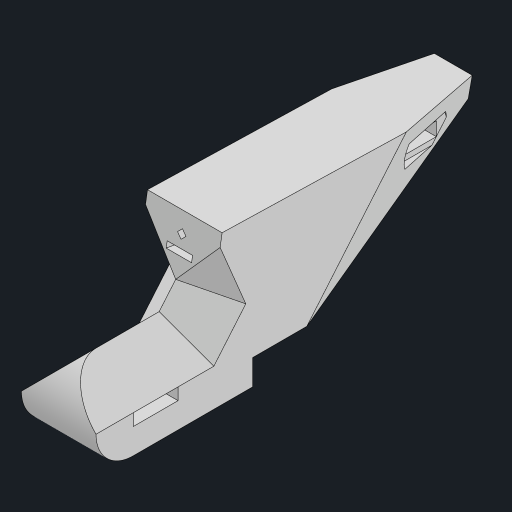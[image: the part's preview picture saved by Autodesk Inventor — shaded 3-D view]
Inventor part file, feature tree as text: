
AUTODESK INVENTOR PART (.ipt)
format: ipt  version: 2023 (Build 270158000, 158)  size: 356,352 bytes
history: native  units: mm
features: extrude x16, sketch x14, other x10, projected_geometry x4
ambient origin geometry x8: Origin, YZ Plane, XZ Plane, XY Plane, X Axis, Y Axis, Z Axis, Center Point
bodies: Body1 (feature_tree)
feature tree (44):
  other  "ソリッド1"
  extrude  "押し出し1"  Depth=0.261799mm
  other  "作業平面1"
  other  "作業平面3"
  extrude  "押し出し5"  Depth=37.0mm
  extrude  "押し出し6"  Depth=25.0mm
  other  "おでこ"
  other  "作業平面4"
  extrude  "押し出し7"  Depth=22.68928mm
  other  "作業平面5"
  extrude  "押し出し8"  Depth=1.658063mm
  extrude  "押し出し9"  Depth=60.0mm
  other  "作業平面9"
  extrude  "押し出し16"  Depth=3.0mm
  other  "作業平面11"
  extrude  "押し出し11"  Depth=80.0mm
  extrude  "押し出し12"  Depth=180.0mm
  extrude  "押し出し13"  Depth=25.0mm
  extrude  "押し出し15"  Depth=5.0mm
  extrude  "貫通"  Depth=180.0mm
  extrude  "25mm"  Depth=15.0mm
  other  "作業平面12"
  extrude  "押し出し24"  Depth=50.0mm TaperAngle=0.0deg
  other  "作業平面13"
  extrude  "押し出し25"  Depth=50.0mm
  extrude  "右半分"  Depth=25.0mm TaperAngle=90.0deg
  sketch  "スケッチ1"
  sketch  "スケッチ5"
  sketch  "スケッチ6"
  sketch  "スケッチ8"
  sketch  "スケッチ9"
  sketch  "スケッチ10"
  projected_geometry  "投影ループ1"
  projected_geometry  "投影ループ2"
  sketch  "スケッチ12"
  sketch  "スケッチ14"
  sketch  "スケッチ16"
  projected_geometry  "投影ループ3"
  sketch  "スケッチ20"
  sketch  "スケッチ21"
  sketch  "スケッチ22"
  sketch  "スケッチ24"
  projected_geometry  "投影ループ5"
  sketch  "スケッチ25"
